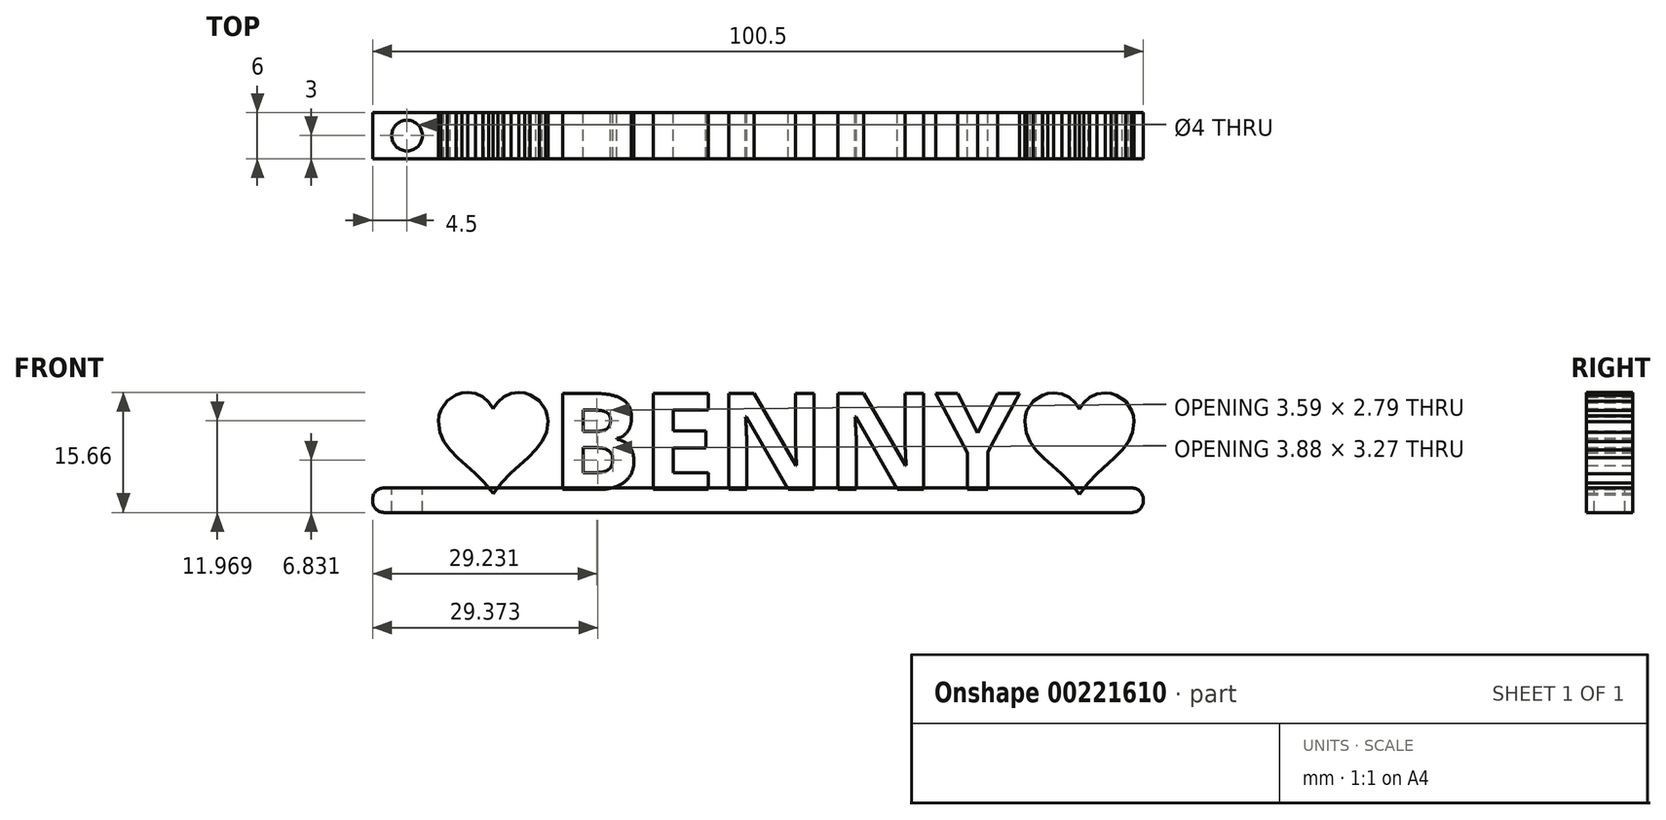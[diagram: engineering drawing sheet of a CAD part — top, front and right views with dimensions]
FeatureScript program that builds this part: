
annotation { "Feature Type Name" : "Feature", "Feature Type Description" : "" }
export const myFeature = defineFeature(function(context is Context, id is Id, definition is map)
    precondition{}
    {
        {
            var Q0;
            Q0=qCreatedBy(makeId("Front.planeOp"),FACE);
            var sketch = newSketch(context, id + "F0", { "sketchPlane" : qUnion([Q0])});
            skText(sketch, "E0", { "text": "   BENNY", "fontName": "OpenSans-Bold.ttf"});
            skLineSegment(sketch, "E1", {"start": v(60.1, 12.6) * mm, "end": v(59.34, 12.52) * mm});
            skLineSegment(sketch, "E2", {"start": v(59.34, 12.52) * mm, "end": v(58.64, 12.3) * mm});
            skLineSegment(sketch, "E3", {"start": v(58.64, 12.3) * mm, "end": v(57.44, 11.5) * mm});
            skLineSegment(sketch, "E4", {"start": v(57.44, 11.5) * mm, "end": v(56.63, 10.3) * mm});
            skLineSegment(sketch, "E5", {"start": v(56.63, 10.3) * mm, "end": v(56.41, 9.59) * mm});
            skLineSegment(sketch, "E6", {"start": v(56.41, 9.59) * mm, "end": v(56.33, 8.83) * mm});
            skLineSegment(sketch, "E7", {"start": v(56.33, 8.83) * mm, "end": v(56.52, 7.39) * mm});
            skLineSegment(sketch, "E8", {"start": v(56.52, 7.39) * mm, "end": v(57.04, 6.16) * mm});
            skLineSegment(sketch, "E9", {"start": v(57.04, 6.16) * mm, "end": v(57.83, 5.08) * mm});
            skLineSegment(sketch, "E10", {"start": v(57.83, 5.08) * mm, "end": v(58.81, 4.08) * mm});
            skLineSegment(sketch, "E11", {"start": v(58.81, 4.08) * mm, "end": v(61.11, 2.03) * mm});
            skLineSegment(sketch, "E12", {"start": v(61.11, 2.03) * mm, "end": v(62.3, 0.82) * mm});
            skLineSegment(sketch, "E13", {"start": v(62.3, 0.82) * mm, "end": v(63.42, -0.59) * mm});
            skLineSegment(sketch, "E14", {"start": v(63.42, -0.59) * mm, "end": v(63.46, -0.65) * mm});
            skLineSegment(sketch, "E15", {"start": v(63.46, -0.65) * mm, "end": v(63.5, -0.59) * mm});
            skLineSegment(sketch, "E16", {"start": v(63.5, -0.59) * mm, "end": v(64.58, 0.82) * mm});
            skLineSegment(sketch, "E17", {"start": v(64.58, 0.82) * mm, "end": v(65.75, 2.03) * mm});
            skLineSegment(sketch, "E18", {"start": v(65.75, 2.03) * mm, "end": v(68.05, 4.12) * mm});
            skLineSegment(sketch, "E19", {"start": v(68.05, 4.12) * mm, "end": v(69.05, 5.13) * mm});
            skLineSegment(sketch, "E20", {"start": v(69.05, 5.13) * mm, "end": v(69.86, 6.21) * mm});
            skLineSegment(sketch, "E21", {"start": v(69.86, 6.21) * mm, "end": v(70.4, 7.42) * mm});
            skLineSegment(sketch, "E22", {"start": v(70.4, 7.42) * mm, "end": v(70.59, 8.83) * mm});
            skLineSegment(sketch, "E23", {"start": v(70.59, 8.83) * mm, "end": v(70.51, 9.59) * mm});
            skLineSegment(sketch, "E24", {"start": v(70.51, 9.59) * mm, "end": v(70.3, 10.3) * mm});
            skLineSegment(sketch, "E25", {"start": v(70.3, 10.3) * mm, "end": v(69.48, 11.5) * mm});
            skLineSegment(sketch, "E26", {"start": v(69.48, 11.5) * mm, "end": v(68.29, 12.3) * mm});
            skLineSegment(sketch, "E27", {"start": v(68.29, 12.3) * mm, "end": v(67.58, 12.52) * mm});
            skLineSegment(sketch, "E28", {"start": v(67.58, 12.52) * mm, "end": v(66.82, 12.6) * mm});
            skLineSegment(sketch, "E29", {"start": v(66.82, 12.6) * mm, "end": v(65.76, 12.44) * mm});
            skLineSegment(sketch, "E30", {"start": v(65.76, 12.44) * mm, "end": v(64.82, 12.01) * mm});
            skLineSegment(sketch, "E31", {"start": v(64.82, 12.01) * mm, "end": v(64.04, 11.35) * mm});
            skLineSegment(sketch, "E32", {"start": v(64.04, 11.35) * mm, "end": v(63.46, 10.5) * mm});
            skLineSegment(sketch, "E33", {"start": v(63.46, 10.5) * mm, "end": v(62.88, 11.35) * mm});
            skLineSegment(sketch, "E34", {"start": v(62.88, 11.35) * mm, "end": v(62.1, 12.01) * mm});
            skLineSegment(sketch, "E35", {"start": v(62.1, 12.01) * mm, "end": v(61.16, 12.44) * mm});
            skLineSegment(sketch, "E36", {"start": v(61.16, 12.44) * mm, "end": v(60.1, 12.6) * mm});
            skLineSegment(sketch, "E37", {"start": v(56.8, 12.65) * mm, "end": v(73.13, 12.65) * mm, "construction": true});
            skLineSegment(sketch, "E38", {"start": v(-16.32, 12.66) * mm, "end": v(-17.08, 12.59) * mm});
            skLineSegment(sketch, "E39", {"start": v(-17.08, 12.59) * mm, "end": v(-17.78, 12.37) * mm});
            skLineSegment(sketch, "E40", {"start": v(-17.78, 12.37) * mm, "end": v(-18.98, 11.56) * mm});
            skLineSegment(sketch, "E41", {"start": v(-18.98, 11.56) * mm, "end": v(-19.79, 10.36) * mm});
            skLineSegment(sketch, "E42", {"start": v(-19.79, 10.36) * mm, "end": v(-20, 9.65) * mm});
            skLineSegment(sketch, "E43", {"start": v(-20, 9.65) * mm, "end": v(-20.09, 8.9) * mm});
            skLineSegment(sketch, "E44", {"start": v(-20.09, 8.9) * mm, "end": v(-19.9, 7.45) * mm});
            skLineSegment(sketch, "E45", {"start": v(-19.9, 7.45) * mm, "end": v(-19.38, 6.22) * mm});
            skLineSegment(sketch, "E46", {"start": v(-19.38, 6.22) * mm, "end": v(-18.6, 5.15) * mm});
            skLineSegment(sketch, "E47", {"start": v(-18.6, 5.15) * mm, "end": v(-17.6, 4.15) * mm});
            skLineSegment(sketch, "E48", {"start": v(-17.6, 4.15) * mm, "end": v(-15.31, 2.09) * mm});
            skLineSegment(sketch, "E49", {"start": v(-15.31, 2.09) * mm, "end": v(-14.13, 0.89) * mm});
            skLineSegment(sketch, "E50", {"start": v(-14.13, 0.89) * mm, "end": v(-13, -0.52) * mm});
            skLineSegment(sketch, "E51", {"start": v(-13, -0.52) * mm, "end": v(-12.96, -0.59) * mm});
            skLineSegment(sketch, "E52", {"start": v(-12.96, -0.59) * mm, "end": v(-12.92, -0.52) * mm});
            skLineSegment(sketch, "E53", {"start": v(-12.92, -0.52) * mm, "end": v(-11.84, 0.89) * mm});
            skLineSegment(sketch, "E54", {"start": v(-11.84, 0.89) * mm, "end": v(-10.67, 2.1) * mm});
            skLineSegment(sketch, "E55", {"start": v(-10.67, 2.1) * mm, "end": v(-8.37, 4.19) * mm});
            skLineSegment(sketch, "E56", {"start": v(-8.37, 4.19) * mm, "end": v(-7.37, 5.2) * mm});
            skLineSegment(sketch, "E57", {"start": v(-7.37, 5.2) * mm, "end": v(-6.56, 6.28) * mm});
            skLineSegment(sketch, "E58", {"start": v(-6.56, 6.28) * mm, "end": v(-6.03, 7.49) * mm});
            skLineSegment(sketch, "E59", {"start": v(-6.03, 7.49) * mm, "end": v(-5.83, 8.9) * mm});
            skLineSegment(sketch, "E60", {"start": v(-5.83, 8.9) * mm, "end": v(-5.91, 9.65) * mm});
            skLineSegment(sketch, "E61", {"start": v(-5.91, 9.65) * mm, "end": v(-6.13, 10.36) * mm});
            skLineSegment(sketch, "E62", {"start": v(-6.13, 10.36) * mm, "end": v(-6.94, 11.56) * mm});
            skLineSegment(sketch, "E63", {"start": v(-6.94, 11.56) * mm, "end": v(-8.13, 12.37) * mm});
            skLineSegment(sketch, "E64", {"start": v(-8.13, 12.37) * mm, "end": v(-8.84, 12.59) * mm});
            skLineSegment(sketch, "E65", {"start": v(-8.84, 12.59) * mm, "end": v(-9.6, 12.66) * mm});
            skLineSegment(sketch, "E66", {"start": v(-9.6, 12.66) * mm, "end": v(-10.66, 12.5) * mm});
            skLineSegment(sketch, "E67", {"start": v(-10.66, 12.5) * mm, "end": v(-11.6, 12.08) * mm});
            skLineSegment(sketch, "E68", {"start": v(-11.6, 12.08) * mm, "end": v(-12.38, 11.41) * mm});
            skLineSegment(sketch, "E69", {"start": v(-12.38, 11.41) * mm, "end": v(-12.96, 10.56) * mm});
            skLineSegment(sketch, "E70", {"start": v(-12.96, 10.56) * mm, "end": v(-13.54, 11.41) * mm});
            skLineSegment(sketch, "E71", {"start": v(-13.54, 11.41) * mm, "end": v(-14.32, 12.08) * mm});
            skLineSegment(sketch, "E72", {"start": v(-14.32, 12.08) * mm, "end": v(-15.26, 12.5) * mm});
            skLineSegment(sketch, "E73", {"start": v(-15.26, 12.5) * mm, "end": v(-16.32, 12.66) * mm});
            const initialGuessF0  = {"E0": [-0.0192, 0, 1, 0, 0.01265]};
            skSetInitialGuess(sketch, initialGuessF0);
            skSolve(sketch);
        }
        {
            var Q0;
            Q0=qSketchRegion(id+"F0",true);
            extrude(context, id + "F1", {"entities" : qUnion([Q0]), "endBound" : BoundingType.SYMMETRIC, "depth" : 6 * mm});
        }
        {
            var Q0;
            Q0=qCreatedBy(makeId("Top.planeOp"),FACE);
            var sketch = newSketch(context, id + "F2", { "sketchPlane" : qUnion([Q0])});
            skLineSegment(sketch, "E74.bottom", {"start": v(-21.2, 3) * mm, "end": v(71.8, 3) * mm});
            skLineSegment(sketch, "E74.top", {"start": v(-21.2, -3) * mm, "end": v(71.8, -3) * mm});
            skLineSegment(sketch, "E74.left", {"start": v(-21.2, 3) * mm, "end": v(-21.2, -3) * mm});
            skLineSegment(sketch, "E74.right", {"start": v(71.8, 3) * mm, "end": v(71.8, -3) * mm});
            skSolve(sketch);
        }
        {
            var Q0;
            Q0=makeQuery(id+"F2.imprint","IMPRINT",FACE,{"disambiguationData":[TD([[makeQuery(id+"F2.imprint","IMPRINT",EDGE,{"derivedFrom":sQuery(id+"F2.wireOp",EDGE,"E74.bottom")}),-1.0]])]});
            extrude(context, id + "F3", {"entities" : qUnion([Q0]), "depth" : 0.2 * mm});
        }
        {
            var Q0;
            Q0=makeQuery(id+"F3.opExtrude","CAP_FACE",FACE,{"disambiguationData":[OSD([sQuery(id+"F2.wireOp",EDGE,"E74.bottom"),sQuery(id+"F2.wireOp",EDGE,"E74.top"),sQuery(id+"F2.wireOp",EDGE,"E74.left"),sQuery(id+"F2.wireOp",EDGE,"E74.right")])],"isStart":true});
            extrude(context, id + "F4", {"entities" : qUnion([Q0]), "depth" : 3 * mm});
        }
        {
            var Q0;
            {var subQ0=sQuery(id+"F2.wireOp",EDGE,"E74.left");Q0=makeQuery(id+"FaVoHrOpcFZXiYX_6.opBoolean","MERGE",FACE,{"derivedFrom":[makeQuery(id+"F3.opExtrude","SWEPT_FACE",FACE,{"disambiguationData":[OSD([subQ0])]}),makeQuery(id+"F4.opExtrude","SWEPT_FACE",FACE,{"disambiguationData":[OSD([subQ0])]})]});}
            var sketch = newSketch(context, id + "F5", { "sketchPlane" : qUnion([Q0])});
            skLineSegment(sketch, "E75.bottom", {"start": v(-3, -3) * mm, "end": v(3, -3) * mm});
            skLineSegment(sketch, "E75.top", {"start": v(-3, 0.2) * mm, "end": v(3, 0.2) * mm});
            skLineSegment(sketch, "E75.left", {"start": v(-3, -3) * mm, "end": v(-3, 0.2) * mm});
            skLineSegment(sketch, "E75.right", {"start": v(3, -3) * mm, "end": v(3, 0.2) * mm});
            skSolve(sketch);
        }
        {
            var Q0;
            Q0=qSketchRegion(id+"F5",true);
            extrude(context, id + "F6", {"entities" : qUnion([Q0]), "operationType" : NewBodyOperationType.ADD, "depth" : 7.5 * mm});
        }
        {
            var Q0;
            Q0=makeQuery(id+"F6.opExtrude","CAP_EDGE",EDGE,{"disambiguationData":[OSD([sQuery(id+"F5.wireOp",EDGE,"E75.bottom")])],"isStart":false});
            var Q1;
            Q1=makeQuery(id+"F6.opExtrude","CAP_EDGE",EDGE,{"disambiguationData":[OSD([sQuery(id+"F5.wireOp",EDGE,"E75.top")])],"isStart":false});
            var Q2;
            Q2=makeQuery(id+"F4.opExtrude","CAP_EDGE",EDGE,{"disambiguationData":[OSD([sQuery(id+"F2.wireOp",EDGE,"E74.right")])],"isStart":false});
            fillet(context, id + "F7", {"entities" : qUnion([Q0, Q1, Q2]), "radius" : 1.5 * mm, "tangentPropagation" : true, "allowEdgeOverflow" : false});
        }
        {
            var Q0;
            {var subQ19=sQuery(id+"F2.wireOp",EDGE,"E74.top");var subQ20=sQuery(id+"F2.wireOp",EDGE,"E74.bottom");var subQ63=sQuery(id+"F0.wireOp",EDGE,"E0.sketch_text.stroke-2");var subQ66=sQuery(id+"F2.wireOp",EDGE,"E74.left");Q0=makeQuery(id+"F6.boolean.opBoolean","MERGE",FACE,{"derivedFrom":[makeQuery(id+"FaVoHrOpcFZXiYX_6.opBoolean","SPLIT",FACE,{"disambiguationData":[TD([makeQuery(id+"F1.opExtrude","SWEPT_FACE",FACE,{"disambiguationData":[OSD([subQ63])]})])],"derivedFrom":makeQuery(id+"F3.opExtrude","CAP_FACE",FACE,{"disambiguationData":[OSD([subQ20,subQ19,subQ66,sQuery(id+"F2.wireOp",EDGE,"E74.right")])],"isStart":false})}),makeQuery(id+"F6.opExtrude","SWEPT_FACE",FACE,{"disambiguationData":[OSD([sQuery(id+"F5.wireOp",EDGE,"E75.top")])]})]});}
            var sketch = newSketch(context, id + "F8", { "sketchPlane" : qUnion([Q0])});
            skCircle(sketch, "E76", {"center": v(-24.2, 0) * mm, "radius": 2 * mm});
            skSolve(sketch);
        }
        {
            var Q0;
            Q0=makeQuery(id+"F8.imprint","IMPRINT",FACE,{"disambiguationData":[TD([[makeQuery(id+"F8.imprint","IMPRINT",EDGE,{"derivedFrom":sQuery(id+"F8.wireOp",EDGE,"E76")}),1.0]])]});
            extrude(context, id + "F9", {"entities" : qUnion([Q0]), "operationType" : NewBodyOperationType.REMOVE, "oppositeDirection" : true, "depth" : 4 * mm});
        }
        {
            var Q0;
            Q0=makeQuery(id+"F3.opExtrude","CAP_EDGE",EDGE,{"disambiguationData":[OSD([sQuery(id+"F2.wireOp",EDGE,"E74.right")])],"isStart":false});
            fillet(context, id + "F10", {"entities" : qUnion([Q0]), "radius" : 1.5 * mm, "tangentPropagation" : true, "allowEdgeOverflow" : false});
        }
    });
